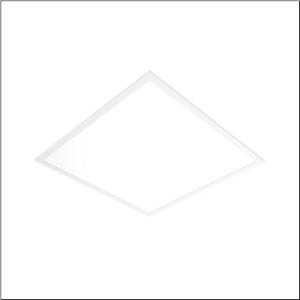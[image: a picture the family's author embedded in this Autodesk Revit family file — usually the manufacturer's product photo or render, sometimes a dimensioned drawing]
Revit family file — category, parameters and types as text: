
# Revit family: apollon_r__41_51mh12w72322_d90e
name_source: partatom
category: Lighting Fixtures
units: mm (PartAtom-declared; Revit-internal decimal feet)

## family parameters
Cut with Voids When Loaded = No
Host = Face
Light Source = No
Part Type = Normal
Room Calculation Point = No
Round Connector Dimension = Use Diameter
Shared = No

## types (1)
- Apollon® 41 (1 x LED, 3550 lm, 35 W, 3000K)
    Apparent Load = 35 VA
    CIE Flux Codes = 63 87 97 100 100
    Color Rendering = 80
    Color Temperature = 3000K
    Default Elevation = 1800 mm
    Description = Apollon® 41, office luminaire, primary optical cover: prismatic diffuser, of PS, light emission: direct distribution, primary light characteristic: symmetric, installation type: lay-in mounting, LED, rated luminous flux: 3.550lm, luminous efficacy: 100lm/W, light colour: 830, colour temperature: 3000K, control gear: ECG, with terminal, 3-pole, mains connection: 220..240V, AC, 50/60Hz, rated input power: 35W, housing, of aluminium section, traffic white (RAL 9016), module: M600, length: 595mm, width: 595mm, height: 32mm, housing upper side, of sheet steel, protection rating (complete): IP20, protection rating (lamp compartment, on room side): IP40, insulation class (complete): insulation class II (safety insulation), certification: CE, ENEC, permissible operating ambient temperature: -20..+40°C, packaging unit: 1 piece
    Height = 0 mm  [stored 0 ft]
    Lamp = 1 x LED
    Lamp Light Flux = 3550 lm
    Lamp Power = 35 W
    Lamp count = 1
    Length = 595 mm
    Luminous efficacy = 101 lm/W
    Manufacturer = Siteco
    ModVariant = No
    Model = 51MH12W72322
    Mounting Place = Ceiling
    Mounting Type = Recessed
    Number of Poles = 1
    OnlyDefault = Yes
    Power Factor = 1
    Product Name = Apollon® 41
    Product group = office luminaire | ceiling recessed
    ProductGroupID = 401
    Protection Class = Protection class II
    Protection Degree = IP 20
    RLX_Detail_Level = 1
    RLX_Emergency_Light_Flux = 0 lm
    RLX_Emergency_Type = 0
    RLX_Emergency_Type_DB = No
    RlxData = <blob elided: 14829 chars, md5=ab41b2ac>
    Socket = socket
    Standby Power = 0 W
    System Light Flux = 3550 lm
    System Power = 35 W
    Type Comments = Product without accessories
    Type Image = l_1291024.jpg
    URL = http://relux.com
    VarID = ---
    Voltage = 0 V
    Weight = 0.00 kg
    Width = 595 mm

note: [stored X ft] marks values corroborated as IEEE doubles in the binary element streams (Revit-internal decimal feet)

## geometry (parser evidence)
native form markers: Sweep x10
no freeform markers — native parametric forms only
